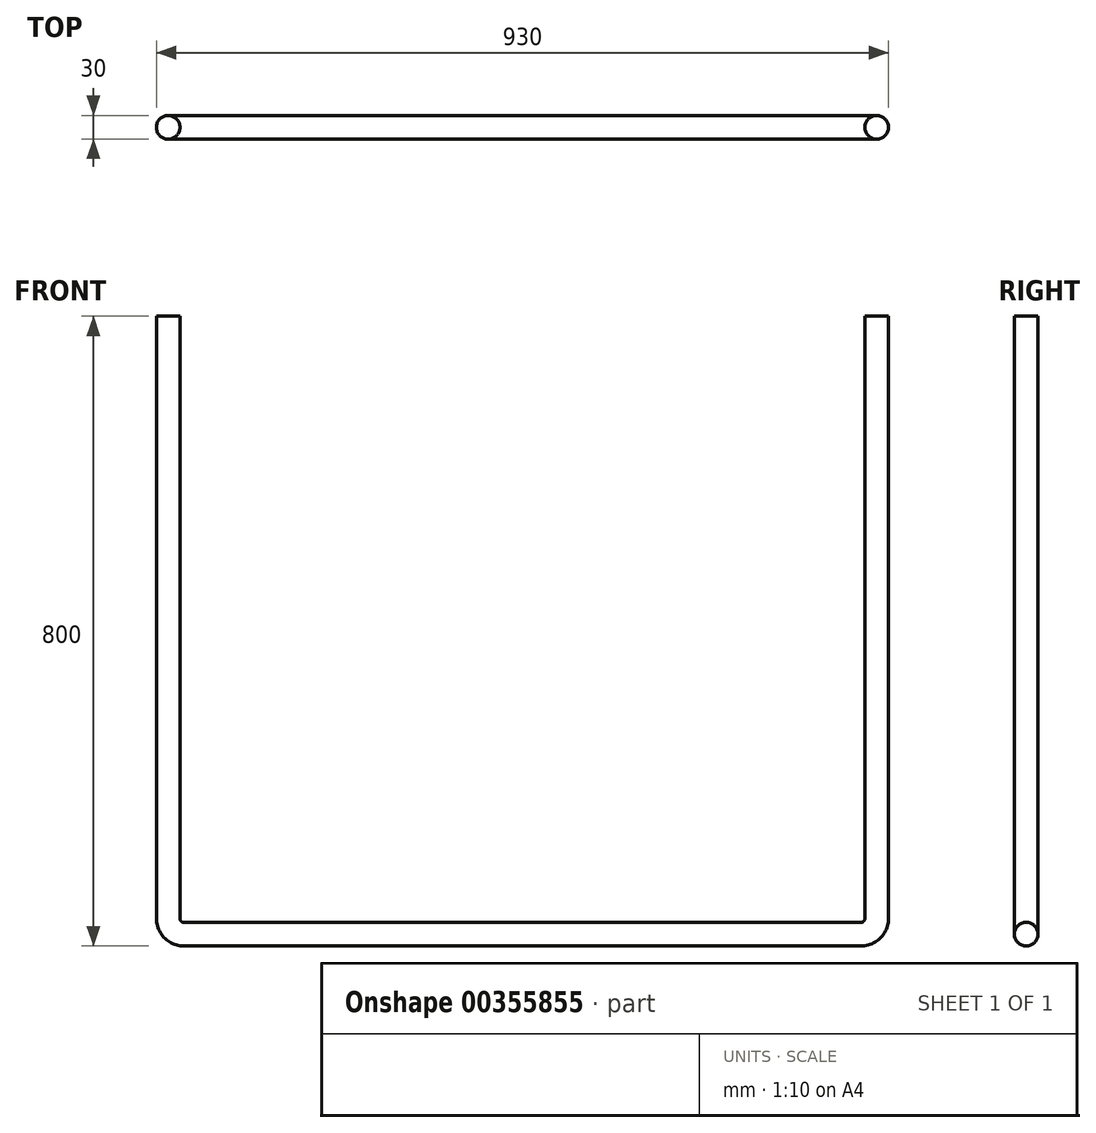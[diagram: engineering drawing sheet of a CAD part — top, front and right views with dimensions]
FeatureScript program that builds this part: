
annotation { "Feature Type Name" : "Feature", "Feature Type Description" : "" }
export const myFeature = defineFeature(function(context is Context, id is Id, definition is map)
    precondition{}
    {
        {
            var Q0;
            Q0=qCreatedBy(makeId("Top.planeOp"),FACE);
            var sketch = newSketch(context, id + "F0", { "sketchPlane" : qUnion([Q0])});
            skCircle(sketch, "E0", {"center": v(-399.07, -36.91) * mm, "radius": 15 * mm});
            skCircle(sketch, "E1", {"center": v(500.93, -36.91) * mm, "radius": 15 * mm});
            skPoint(sketch, "E2.orphan", {"position": v(485.93, -36.91) * mm});
            skPoint(sketch, "E3.trimOffspring.end.orphan", {"position": v(515.93, -36.91) * mm});
            skPoint(sketch, "E4.orphan", {"position": v(-414.07, -36.91) * mm});
            skLineSegment(sketch, "E5", {"start": v(-399.07, -36.91) * mm, "end": v(500.93, -36.91) * mm});
            skSolve(sketch);
        }
        {
            var Q0;
            Q0=qCreatedBy(makeId("Front.planeOp"),FACE);
            var Q1;
            Q1=sQuery(id+"F0.wireOp",VERTEX,"E0.center");
            cPlane(context, id + "F1", {"entities" : qUnion([Q0, Q1]), "cplaneType" : CPlaneType.PLANE_POINT, "offset" : 25 * mm, "width" : 150 * mm, "height" : 150 * mm});
        }
        {
            var Q0;
            Q0=qCreatedBy(id+"F1.planeOp",FACE);
            var sketch = newSketch(context, id + "F2", { "sketchPlane" : qUnion([Q0])});
            skLineSegment(sketch, "E6.0", {"start": v(-414.07, 0) * mm, "end": v(-384.07, 0) * mm});
            skLineSegment(sketch, "E7.0", {"start": v(485.93, 0) * mm, "end": v(515.93, 0) * mm});
            skLineSegment(sketch, "E8.0", {"start": v(500.93, 0) * mm, "end": v(500.93, -765) * mm});
            skLineSegment(sketch, "E8.1", {"start": v(-379.07, -785) * mm, "end": v(480.93, -785) * mm});
            skLineSegment(sketch, "E8.2", {"start": v(-399.07, 0) * mm, "end": v(-399.07, -765) * mm});
            skPoint(sketch, "E9.visualSharp", {"position": v(-399.07, -785) * mm});
            skArc(sketch, "E9.filletArc", {"start": v(-399.07, -765) * mm, "mid": v(-393.22, -779.14) * mm, "end": v(-379.07, -785) * mm});
            skPoint(sketch, "E10.visualSharp", {"position": v(500.93, -785) * mm});
            skArc(sketch, "E10.filletArc", {"start": v(480.93, -785) * mm, "mid": v(495.07, -779.14) * mm, "end": v(500.93, -765) * mm});
            skSolve(sketch);
        }
        {
            var Q0;
            Q0=makeQuery(id+"F0.imprint","IMPRINT",FACE,{"disambiguationData":[TD([[makeQuery(id+"F0.imprint","IMPRINT",EDGE,{"derivedFrom":sQuery(id+"F0.wireOp",EDGE,"E0")}),1.0]])]});
            var Q1;
            Q1=sQuery(id+"F2.wireOp",EDGE,"E8.2");
            var Q2;
            Q2=sQuery(id+"F2.wireOp",EDGE,"E9.filletArc");
            var Q3;
            Q3=sQuery(id+"F2.wireOp",EDGE,"E8.1");
            var Q4;
            Q4=sQuery(id+"F2.wireOp",EDGE,"E10.filletArc");
            var Q5;
            Q5=sQuery(id+"F2.wireOp",EDGE,"E8.0");
            sweep(context, id + "F3", {"profiles" : qUnion([Q0]), "path" : qUnion([Q1, Q2, Q3, Q4, Q5])});
        }
    });
